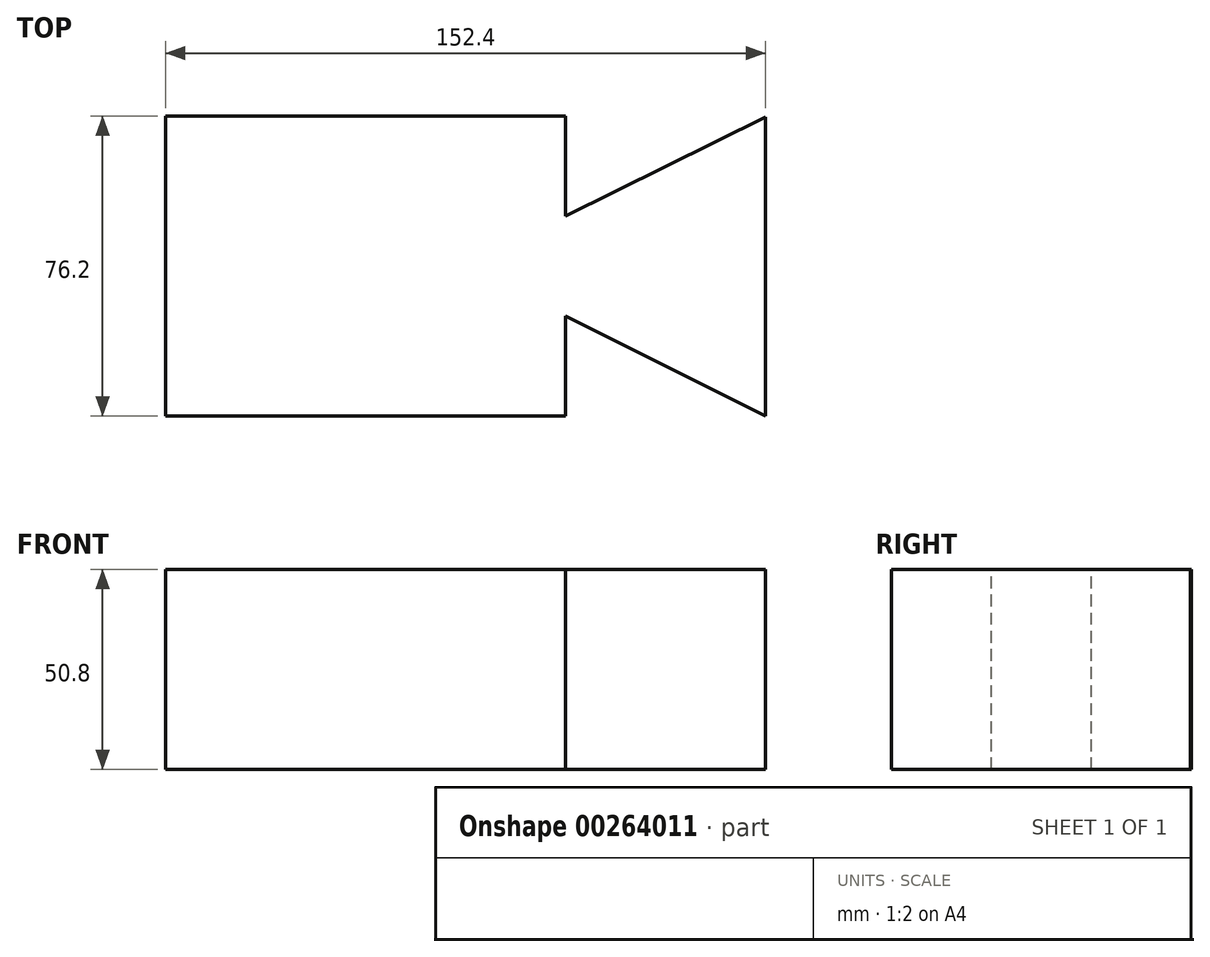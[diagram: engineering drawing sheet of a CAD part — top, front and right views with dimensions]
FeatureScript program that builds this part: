
annotation { "Feature Type Name" : "Feature", "Feature Type Description" : "" }
export const myFeature = defineFeature(function(context is Context, id is Id, definition is map)
    precondition{}
    {
        {
            var Q0;
            Q0=qCreatedBy(makeId("Top.planeOp"),FACE);
            var sketch = newSketch(context, id + "F0", { "sketchPlane" : qUnion([Q0])});
            skLineSegment(sketch, "E0.bottom", {"start": v(0, 0) * mm, "end": v(-101.6, 0) * mm});
            skLineSegment(sketch, "E0.top", {"start": v(0, 76.2) * mm, "end": v(-101.6, 76.2) * mm});
            skLineSegment(sketch, "E0.left", {"start": v(0, 0) * mm, "end": v(0, 76.2) * mm});
            skLineSegment(sketch, "E0.right", {"start": v(-101.6, 0) * mm, "end": v(-101.6, 76.2) * mm});
            skLineSegment(sketch, "E1", {"start": v(0, 0) * mm, "end": v(0, 25.4) * mm, "construction": true});
            skLineSegment(sketch, "E2", {"start": v(0, 76.2) * mm, "end": v(0, 50.8) * mm, "construction": true});
            skLineSegment(sketch, "E3", {"start": v(0, 25.4) * mm, "end": v(50.8, 0) * mm});
            skLineSegment(sketch, "E4", {"start": v(50.8, 0) * mm, "end": v(50.8, 75.97) * mm});
            skLineSegment(sketch, "E5", {"start": v(50.8, 75.97) * mm, "end": v(0, 50.8) * mm});
            skSolve(sketch);
        }
        {
            var Q0;
            {var subQ3=sQuery(id+"F0.wireOp",EDGE,"E0.bottom");Q0=makeQuery(id+"F0.imprint","IMPRINT",FACE,{"disambiguationData":[TD([[makeQuery(id+"F0.imprint","IMPRINT",EDGE,{"derivedFrom":subQ3}),-1.0]])]});}
            var Q1;
            {var subQ0=sQuery(id+"F0.wireOp",EDGE,"E3");Q1=makeQuery(id+"F0.imprint","IMPRINT",FACE,{"disambiguationData":[TD([[makeQuery(id+"F0.imprint","IMPRINT",EDGE,{"derivedFrom":subQ0}),1.0]])]});}
            extrude(context, id + "F1", {"entities" : qUnion([Q0, Q1]), "oppositeDirection" : true, "depth" : 50.8 * mm});
        }
    });
